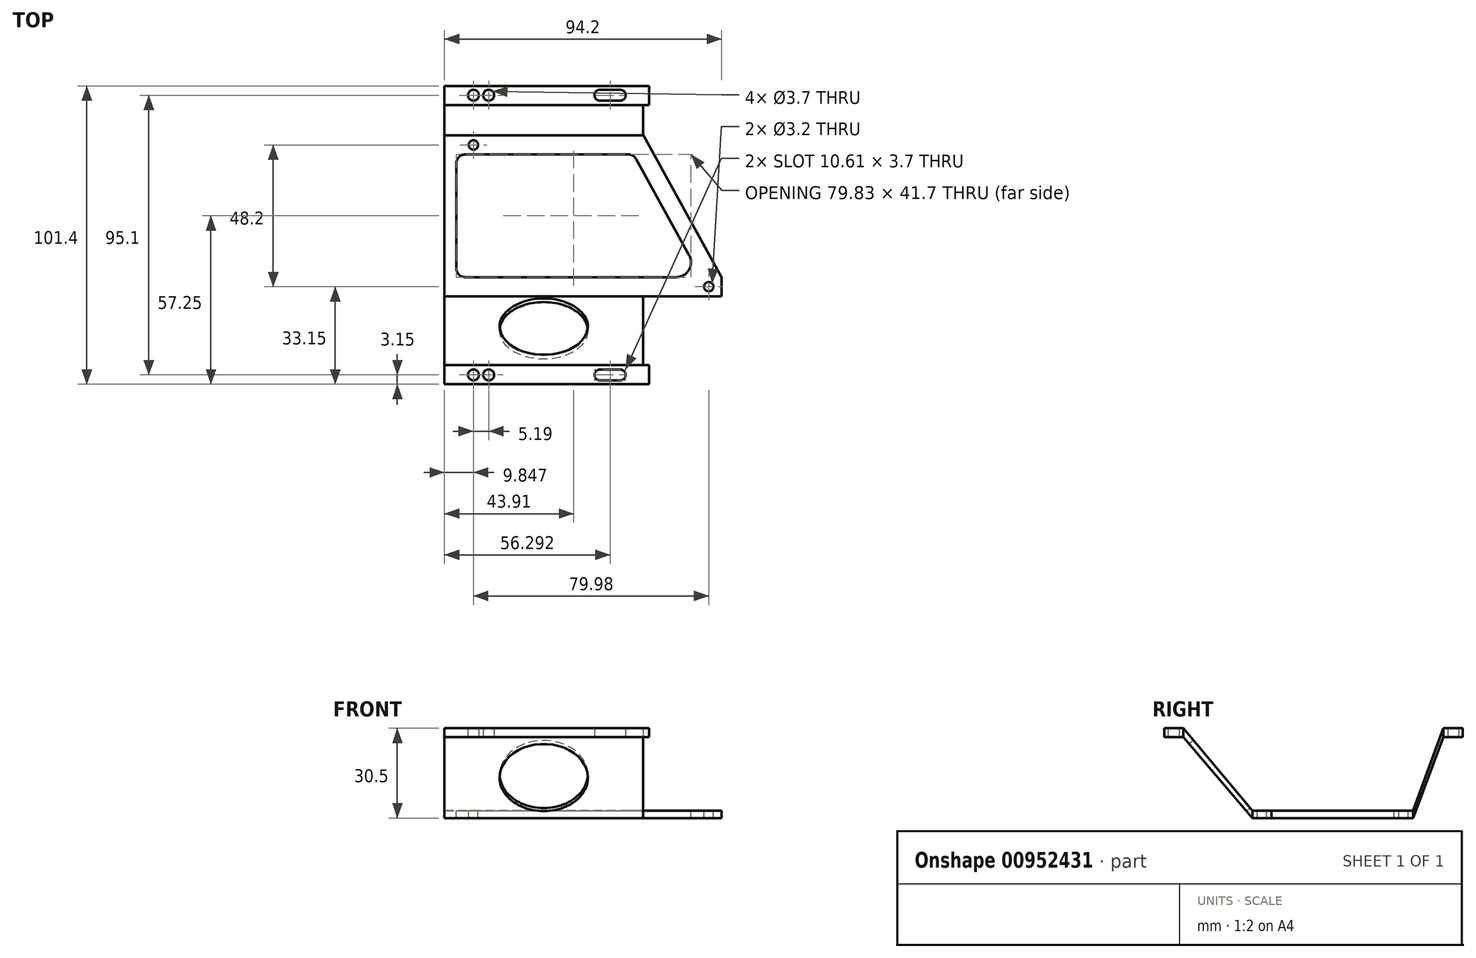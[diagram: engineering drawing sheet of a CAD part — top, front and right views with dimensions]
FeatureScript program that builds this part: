
annotation { "Feature Type Name" : "Feature", "Feature Type Description" : "" }
export const myFeature = defineFeature(function(context is Context, id is Id, definition is map)
    precondition{}
    {
        {
            var Q0;
            Q0=qCreatedBy(makeId("Top.planeOp"),FACE);
            var sketch = newSketch(context, id + "F0", { "sketchPlane" : qUnion([Q0])});
            skLineSegment(sketch, "E0.bottom", {"start": v(-119.45, 40.08) * mm, "end": v(-9.45, 40.08) * mm});
            skLineSegment(sketch, "E0.top", {"start": v(-119.45, -61.32) * mm, "end": v(-9.45, -61.32) * mm});
            skLineSegment(sketch, "E0.left", {"start": v(-119.45, 40.08) * mm, "end": v(-119.45, -61.32) * mm});
            skLineSegment(sketch, "E0.right", {"start": v(-9.45, 40.08) * mm, "end": v(-9.45, -61.32) * mm});
            skLineSegment(sketch, "E1", {"start": v(-119.45, 36.93) * mm, "end": v(-9.45, 36.93) * mm, "construction": true});
            skLineSegment(sketch, "E2", {"start": v(-119.45, -58.17) * mm, "end": v(-9.45, -58.17) * mm, "construction": true});
            skCircle(sketch, "E3", {"center": v(-94.21, 36.93) * mm, "radius": 1.85 * mm});
            skCircle(sketch, "E4", {"center": v(-99.4, 36.93) * mm, "radius": 1.85 * mm});
            skCircle(sketch, "E5", {"center": v(-99.4, -58.17) * mm, "radius": 1.85 * mm});
            skCircle(sketch, "E6", {"center": v(-94.21, -58.17) * mm, "radius": 1.85 * mm});
            skPoint(sketch, "E7", {"position": v(-58.26, 36.93) * mm});
            skPoint(sketch, "E8", {"position": v(-47.65, 36.93) * mm});
            skLineSegment(sketch, "E9", {"start": v(-56.41, 38.78) * mm, "end": v(-49.5, 38.78) * mm});
            skLineSegment(sketch, "E10", {"start": v(-56.41, 35.08) * mm, "end": v(-49.5, 35.08) * mm});
            skLineSegment(sketch, "E11", {"start": v(-56.41, -56.32) * mm, "end": v(-49.5, -56.32) * mm});
            skLineSegment(sketch, "E12", {"start": v(-56.41, -60.02) * mm, "end": v(-49.5, -60.02) * mm});
            skArc(sketch, "E13", {"start": v(-56.41, -56.32) * mm, "mid": v(-58.26, -58.17) * mm, "end": v(-56.41, -60.02) * mm});
            skArc(sketch, "E14", {"start": v(-56.41, -60.02) * mm, "mid": v(-54.56, -58.17) * mm, "end": v(-56.41, -56.32) * mm, "construction": true});
            skArc(sketch, "E15", {"start": v(-49.5, -56.32) * mm, "mid": v(-51.35, -58.17) * mm, "end": v(-49.5, -60.02) * mm, "construction": true});
            skArc(sketch, "E16", {"start": v(-49.5, -60.02) * mm, "mid": v(-47.65, -58.17) * mm, "end": v(-49.5, -56.32) * mm});
            skArc(sketch, "E17", {"start": v(-49.5, 38.78) * mm, "mid": v(-51.35, 36.93) * mm, "end": v(-49.5, 35.08) * mm, "construction": true});
            skArc(sketch, "E18", {"start": v(-49.5, 35.08) * mm, "mid": v(-47.65, 36.93) * mm, "end": v(-49.5, 38.78) * mm});
            skArc(sketch, "E19", {"start": v(-56.41, 35.08) * mm, "mid": v(-54.56, 36.93) * mm, "end": v(-56.41, 38.78) * mm, "construction": true});
            skArc(sketch, "E20", {"start": v(-56.41, 38.78) * mm, "mid": v(-58.26, 36.93) * mm, "end": v(-56.41, 35.08) * mm});
            skPoint(sketch, "E21", {"position": v(-101.25, 36.93) * mm});
            skPoint(sketch, "E22", {"position": v(-97.55, 36.93) * mm});
            skPoint(sketch, "E23", {"position": v(-96.06, 36.93) * mm});
            skPoint(sketch, "E24", {"position": v(-92.36, 36.93) * mm});
            skPoint(sketch, "E25", {"position": v(-99.4, 38.78) * mm});
            skPoint(sketch, "E26", {"position": v(-99.4, -60.02) * mm});
            skSolve(sketch);
        }
        {
            var Q0;
            Q0=qCreatedBy(makeId("Top.planeOp"),FACE);
            cPlane(context, id + "F1", {"entities" : qUnion([Q0]), "cplaneType" : CPlaneType.OFFSET, "offset" : 25 * mm, "width" : 150 * mm, "height" : 150 * mm});
        }
        {
            var Q0;
            Q0=qCreatedBy(id+"F1.planeOp",FACE);
            var sketch = newSketch(context, id + "F2", { "sketchPlane" : qUnion([Q0])});
            skCircle(sketch, "E27.0", {"center": v(-99.4, 36.93) * mm, "radius": 1.85 * mm});
            skCircle(sketch, "E27.1.0", {"center": v(-99.4, 36.93) * mm, "radius": 1.85 * mm});
            skCircle(sketch, "E27.2.0", {"center": v(-94.21, 36.93) * mm, "radius": 1.85 * mm});
            skLineSegment(sketch, "E27.3.0", {"start": v(-119.45, 40.08) * mm, "end": v(-119.45, -61.32) * mm});
            skLineSegment(sketch, "E27.3.1", {"start": v(-119.45, -61.32) * mm, "end": v(-9.45, -61.32) * mm});
            skLineSegment(sketch, "E27.3.2", {"start": v(-9.45, -61.32) * mm, "end": v(-9.45, 40.08) * mm});
            skLineSegment(sketch, "E27.3.3", {"start": v(-9.45, 40.08) * mm, "end": v(-119.45, 40.08) * mm});
            skArc(sketch, "E27.4.0", {"start": v(-56.41, 38.78) * mm, "mid": v(-58.26, 36.93) * mm, "end": v(-56.41, 35.08) * mm});
            skLineSegment(sketch, "E27.4.1", {"start": v(-56.41, 35.08) * mm, "end": v(-49.5, 35.08) * mm});
            skArc(sketch, "E27.4.2", {"start": v(-49.5, 35.08) * mm, "mid": v(-47.65, 36.93) * mm, "end": v(-49.5, 38.78) * mm});
            skLineSegment(sketch, "E27.4.3", {"start": v(-49.5, 38.78) * mm, "end": v(-56.41, 38.78) * mm});
            skCircle(sketch, "E27.5.0", {"center": v(-99.4, -58.17) * mm, "radius": 1.85 * mm});
            skCircle(sketch, "E27.6.0", {"center": v(-94.21, -58.17) * mm, "radius": 1.85 * mm});
            skArc(sketch, "E27.7.0", {"start": v(-56.41, -56.32) * mm, "mid": v(-58.26, -58.17) * mm, "end": v(-56.41, -60.02) * mm});
            skLineSegment(sketch, "E27.7.1", {"start": v(-56.41, -60.02) * mm, "end": v(-49.5, -60.02) * mm});
            skArc(sketch, "E27.7.2", {"start": v(-49.5, -60.02) * mm, "mid": v(-47.65, -58.17) * mm, "end": v(-49.5, -56.32) * mm});
            skLineSegment(sketch, "E27.7.3", {"start": v(-49.5, -56.32) * mm, "end": v(-56.41, -56.32) * mm});
            skLineSegment(sketch, "E28.bottom", {"start": v(-109.25, 40.08) * mm, "end": v(-39.65, 40.08) * mm});
            skLineSegment(sketch, "E28.top", {"start": v(-109.25, 33.58) * mm, "end": v(-39.65, 33.58) * mm});
            skLineSegment(sketch, "E28.left", {"start": v(-109.25, 40.08) * mm, "end": v(-109.25, 33.58) * mm});
            skLineSegment(sketch, "E28.right", {"start": v(-39.65, 40.08) * mm, "end": v(-39.65, 33.58) * mm});
            skPoint(sketch, "E29", {"position": v(-101.25, 36.93) * mm});
            skPoint(sketch, "E30", {"position": v(-47.65, 36.93) * mm});
            skLineSegment(sketch, "E31.bottom", {"start": v(-109.25, -54.82) * mm, "end": v(-39.65, -54.82) * mm});
            skLineSegment(sketch, "E31.top", {"start": v(-109.25, -61.32) * mm, "end": v(-39.65, -61.32) * mm});
            skLineSegment(sketch, "E31.left", {"start": v(-109.25, -54.82) * mm, "end": v(-109.25, -61.32) * mm});
            skLineSegment(sketch, "E31.right", {"start": v(-39.65, -54.82) * mm, "end": v(-39.65, -61.32) * mm});
            skLineSegment(sketch, "E32.bottom", {"start": v(-114.7, 22.63) * mm, "end": v(-13.1, 22.63) * mm, "construction": true});
            skLineSegment(sketch, "E32.top", {"start": v(-114.7, -30.67) * mm, "end": v(-13.1, -30.67) * mm, "construction": true});
            skLineSegment(sketch, "E32.left", {"start": v(-114.7, 22.63) * mm, "end": v(-114.7, -30.67) * mm, "construction": true});
            skLineSegment(sketch, "E32.right", {"start": v(-13.1, 22.63) * mm, "end": v(-13.1, -30.67) * mm, "construction": true});
            skCircle(sketch, "E33", {"center": v(-99.4, 20.03) * mm, "radius": 1.6 * mm});
            skCircle(sketch, "E34", {"center": v(-19.42, -28.17) * mm, "radius": 1.6 * mm});
            skPoint(sketch, "E35", {"position": v(-99.4, 21.63) * mm});
            skPoint(sketch, "E36", {"position": v(-101, 20.03) * mm});
            skPoint(sketch, "E37", {"position": v(-19.42, -29.77) * mm});
            skPoint(sketch, "E38", {"position": v(-17.82, -28.17) * mm});
            skSolve(sketch);
        }
        {
            var Q0;
            Q0=makeQuery(id+"F2.imprint","IMPRINT",FACE,{"disambiguationData":[TD([[makeQuery(id+"F2.imprint","IMPRINT",EDGE,{"derivedFrom":sQuery(id+"F2.wireOp",EDGE,"E27.0")}),-1.0]])]});
            var Q1;
            Q1=makeQuery(id+"F2.imprint","IMPRINT",FACE,{"disambiguationData":[TD([[makeQuery(id+"F2.imprint","IMPRINT",EDGE,{"derivedFrom":sQuery(id+"F2.wireOp",EDGE,"E27.5.0")}),-1.0]])]});
            extrude(context, id + "F3", {"entities" : qUnion([Q0, Q1]), "depth" : 3 * mm, "offsetDistance" : 25 * mm});
        }
        {
            var Q0;
            Q0=qCreatedBy(makeId("Top.planeOp"),FACE);
            var sketch = newSketch(context, id + "F4", { "sketchPlane" : qUnion([Q0])});
            skCircle(sketch, "E39.0", {"center": v(-99.4, 36.93) * mm, "radius": 1.85 * mm});
            skCircle(sketch, "E39.1", {"center": v(-99.4, 36.93) * mm, "radius": 1.85 * mm});
            skCircle(sketch, "E39.2", {"center": v(-94.21, 36.93) * mm, "radius": 1.85 * mm});
            skLineSegment(sketch, "E39.3", {"start": v(-119.45, 40.08) * mm, "end": v(-119.45, -61.32) * mm});
            skLineSegment(sketch, "E39.4", {"start": v(-119.45, -61.32) * mm, "end": v(-9.45, -61.32) * mm});
            skLineSegment(sketch, "E39.5", {"start": v(-9.45, -61.32) * mm, "end": v(-9.45, 40.08) * mm});
            skLineSegment(sketch, "E39.6", {"start": v(-9.45, 40.08) * mm, "end": v(-119.45, 40.08) * mm});
            skArc(sketch, "E39.7", {"start": v(-56.41, 38.78) * mm, "mid": v(-58.26, 36.93) * mm, "end": v(-56.41, 35.08) * mm});
            skLineSegment(sketch, "E39.8", {"start": v(-56.41, 35.08) * mm, "end": v(-49.5, 35.08) * mm});
            skArc(sketch, "E39.9", {"start": v(-49.5, 35.08) * mm, "mid": v(-47.65, 36.93) * mm, "end": v(-49.5, 38.78) * mm});
            skLineSegment(sketch, "E39.10", {"start": v(-49.5, 38.78) * mm, "end": v(-56.41, 38.78) * mm});
            skCircle(sketch, "E39.11", {"center": v(-99.4, -58.17) * mm, "radius": 1.85 * mm});
            skCircle(sketch, "E39.12", {"center": v(-94.21, -58.17) * mm, "radius": 1.85 * mm});
            skArc(sketch, "E39.13", {"start": v(-56.41, -56.32) * mm, "mid": v(-58.26, -58.17) * mm, "end": v(-56.41, -60.02) * mm});
            skLineSegment(sketch, "E39.14", {"start": v(-56.41, -60.02) * mm, "end": v(-49.5, -60.02) * mm});
            skArc(sketch, "E39.15", {"start": v(-49.5, -60.02) * mm, "mid": v(-47.65, -58.17) * mm, "end": v(-49.5, -56.32) * mm});
            skLineSegment(sketch, "E39.16", {"start": v(-49.5, -56.32) * mm, "end": v(-56.41, -56.32) * mm});
            skLineSegment(sketch, "E39.17", {"start": v(-109.25, 40.08) * mm, "end": v(-39.65, 40.08) * mm});
            skLineSegment(sketch, "E39.18", {"start": v(-109.25, 33.58) * mm, "end": v(-39.65, 33.58) * mm});
            skLineSegment(sketch, "E39.19", {"start": v(-109.25, 40.08) * mm, "end": v(-109.25, 33.58) * mm});
            skLineSegment(sketch, "E39.20", {"start": v(-39.65, 40.08) * mm, "end": v(-39.65, 33.58) * mm});
            skPoint(sketch, "E39.21", {"position": v(-101.25, 36.93) * mm});
            skPoint(sketch, "E39.22", {"position": v(-47.65, 36.93) * mm});
            skLineSegment(sketch, "E39.23", {"start": v(-109.25, -54.82) * mm, "end": v(-39.65, -54.82) * mm});
            skLineSegment(sketch, "E39.24", {"start": v(-109.25, -61.32) * mm, "end": v(-39.65, -61.32) * mm});
            skLineSegment(sketch, "E39.25", {"start": v(-109.25, -54.82) * mm, "end": v(-109.25, -61.32) * mm});
            skLineSegment(sketch, "E39.26", {"start": v(-39.65, -54.82) * mm, "end": v(-39.65, -61.32) * mm});
            skLineSegment(sketch, "E39.27", {"start": v(-114.7, 22.63) * mm, "end": v(-13.1, 22.63) * mm, "construction": true});
            skLineSegment(sketch, "E39.28", {"start": v(-114.7, -30.67) * mm, "end": v(-13.1, -30.67) * mm, "construction": true});
            skLineSegment(sketch, "E39.29", {"start": v(-114.7, 22.63) * mm, "end": v(-114.7, -30.67) * mm, "construction": true});
            skLineSegment(sketch, "E39.30", {"start": v(-13.1, 22.63) * mm, "end": v(-13.1, -30.67) * mm, "construction": true});
            skCircle(sketch, "E39.31", {"center": v(-99.4, 20.03) * mm, "radius": 1.6 * mm});
            skCircle(sketch, "E39.32", {"center": v(-19.42, -28.17) * mm, "radius": 1.6 * mm});
            skPoint(sketch, "E39.33", {"position": v(-99.4, 21.63) * mm});
            skPoint(sketch, "E39.34", {"position": v(-101, 20.03) * mm});
            skPoint(sketch, "E39.35", {"position": v(-19.42, -28.17) * mm});
            skPoint(sketch, "E39.36", {"position": v(-19.42, -29.77) * mm});
            skPoint(sketch, "E39.37", {"position": v(-17.82, -28.17) * mm});
            skLineSegment(sketch, "E40.bottom", {"start": v(-109.25, 23.28) * mm, "end": v(-41.64, 23.28) * mm});
            skLineSegment(sketch, "E40.top", {"start": v(-102.25, 16.78) * mm, "end": v(-46.74, 16.78) * mm});
            skLineSegment(sketch, "E40.left", {"start": v(-109.25, 23.28) * mm, "end": v(-109.25, 16.78) * mm});
            skLineSegment(sketch, "E41.bottom", {"start": v(-109.25, -31.42) * mm, "end": v(-15.05, -31.42) * mm});
            skLineSegment(sketch, "E41.top", {"start": v(-102.25, -24.92) * mm, "end": v(-30.43, -24.92) * mm});
            skLineSegment(sketch, "E41.left", {"start": v(-109.25, -31.42) * mm, "end": v(-109.25, -24.92) * mm});
            skLineSegment(sketch, "E41.right", {"start": v(-15.05, -31.42) * mm, "end": v(-15.05, -24.92) * mm});
            skLineSegment(sketch, "E42", {"start": v(-109.25, 16.78) * mm, "end": v(-109.25, -24.92) * mm});
            skLineSegment(sketch, "E43", {"start": v(-105.25, 13.78) * mm, "end": v(-105.25, -21.92) * mm});
            skLineSegment(sketch, "E44", {"start": v(-41.64, 23.28) * mm, "end": v(-15.05, -24.92) * mm});
            skLineSegment(sketch, "E45", {"start": v(-44.1, 15.23) * mm, "end": v(-26.05, -17.5) * mm});
            skPoint(sketch, "E46.visualSharp", {"position": v(-21.96, -24.92) * mm});
            skArc(sketch, "E46.filletArc", {"start": v(-30.43, -24.92) * mm, "mid": v(-26.12, -22.46) * mm, "end": v(-26.05, -17.5) * mm});
            skPoint(sketch, "E47.visualSharp", {"position": v(-44.97, 16.78) * mm});
            skArc(sketch, "E47.filletArc", {"start": v(-44.1, 15.23) * mm, "mid": v(-45.21, 16.36) * mm, "end": v(-46.74, 16.78) * mm});
            skPoint(sketch, "E48.visualSharp", {"position": v(-105.25, 16.78) * mm});
            skArc(sketch, "E48.filletArc", {"start": v(-102.25, 16.78) * mm, "mid": v(-104.37, 15.9) * mm, "end": v(-105.25, 13.78) * mm});
            skPoint(sketch, "E49.visualSharp", {"position": v(-105.25, -24.92) * mm});
            skArc(sketch, "E49.filletArc", {"start": v(-105.25, -21.92) * mm, "mid": v(-104.37, -24.04) * mm, "end": v(-102.25, -24.92) * mm});
            skSolve(sketch);
        }
        {
            var Q0;
            Q0=makeQuery(id+"F3.opExtrude","SWEPT_FACE",FACE,{"disambiguationData":[OSD([sQuery(id+"F2.wireOp",EDGE,"E28.left")])]});
            var sketch = newSketch(context, id + "F5", { "sketchPlane" : qUnion([Q0])});
            skSolve(sketch);
        }
        {
            var Q0;
            Q0=makeQuery(id+"F4.imprint","IMPRINT",FACE,{"disambiguationData":[TD([[makeQuery(id+"F4.imprint","IMPRINT",EDGE,{"derivedFrom":sQuery(id+"F4.wireOp",EDGE,"E39.31")}),-1.0]])]});
            extrude(context, id + "F6", {"entities" : qUnion([Q0]), "oppositeDirection" : true, "depth" : 2.5 * mm, "offsetDistance" : 25 * mm});
        }
        {
            var Q0;
            {var subQ0=sQuery(id+"F2.wireOp",EDGE,"E28.left");Q0=makeQuery(id+"F5.imprint","IMPRINT",FACE,{"disambiguationData":[TD([[makeQuery(id+"F5.imprint","IMPRINT",EDGE,{"derivedFrom":makeQuery(id+"F3.opExtrude","CAP_EDGE",EDGE,{"disambiguationData":[OSD([subQ0])],"isStart":true})}),1.0]])]});}
            var sketch = newSketch(context, id + "F7", { "sketchPlane" : qUnion([Q0])});
            skPoint(sketch, "E50.0", {"position": v(-40.08, 25) * mm});
            skPoint(sketch, "E50.1", {"position": v(-33.58, 25) * mm});
            skPoint(sketch, "E50.2", {"position": v(-33.58, 28) * mm});
            skPoint(sketch, "E50.3", {"position": v(-23.28, 0) * mm});
            skPoint(sketch, "E50.4", {"position": v(-23.28, -2.5) * mm});
            skPoint(sketch, "E50.5", {"position": v(31.42, -2.5) * mm});
            skPoint(sketch, "E50.6", {"position": v(31.42, 0) * mm});
            skPoint(sketch, "E50.7", {"position": v(54.82, 25) * mm});
            skPoint(sketch, "E50.8", {"position": v(54.82, 28) * mm});
            skPoint(sketch, "E50.9", {"position": v(61.32, 25) * mm});
            skLineSegment(sketch, "E51", {"start": v(-33.58, 28) * mm, "end": v(-23.28, 0) * mm});
            skLineSegment(sketch, "E52", {"start": v(-33.58, 25) * mm, "end": v(-23.28, -2.5) * mm});
            skLineSegment(sketch, "E53", {"start": v(31.42, 0) * mm, "end": v(54.82, 28) * mm});
            skLineSegment(sketch, "E54", {"start": v(31.42, -2.5) * mm, "end": v(54.82, 25) * mm});
            skLineSegment(sketch, "E55", {"start": v(-33.58, 28) * mm, "end": v(-33.58, 25) * mm});
            skLineSegment(sketch, "E56", {"start": v(-23.28, 0) * mm, "end": v(-23.28, -2.5) * mm});
            skLineSegment(sketch, "E57", {"start": v(54.82, 28) * mm, "end": v(54.82, 25) * mm});
            skLineSegment(sketch, "E58", {"start": v(31.42, 0) * mm, "end": v(31.42, -2.5) * mm});
            skSolve(sketch);
        }
        {
            var Q0;
            Q0=makeQuery(id+"F7.imprint","IMPRINT",FACE,{"disambiguationData":[TD([[makeQuery(id+"F7.imprint","IMPRINT",EDGE,{"derivedFrom":sQuery(id+"F7.wireOp",EDGE,"E51")}),-1.0]])]});
            var Q1;
            Q1=makeQuery(id+"F7.imprint","IMPRINT",FACE,{"disambiguationData":[TD([[makeQuery(id+"F7.imprint","IMPRINT",EDGE,{"derivedFrom":sQuery(id+"F7.wireOp",EDGE,"E53")}),-1.0]])]});
            extrude(context, id + "F8", {"entities" : qUnion([Q0, Q1]), "oppositeDirection" : true, "depth" : 67.5 * mm, "offsetDistance" : 25 * mm});
        }
        {
            var Q0;
            Q0=makeQuery(id+"F8.opExtrude","SWEPT_FACE",FACE,{"disambiguationData":[OSD([sQuery(id+"F7.wireOp",EDGE,"E54")])]});
            var sketch = newSketch(context, id + "F9", { "sketchPlane" : qUnion([Q0])});
            skLineSegment(sketch, "E59", {"start": v(-75.5, 54.57) * mm, "end": v(-75.5, 18.46) * mm, "construction": true});
            skLineSegment(sketch, "E60", {"start": v(-109.25, 36.51) * mm, "end": v(-41.75, 36.51) * mm, "construction": true});
            skCircle(sketch, "E61", {"center": v(-75.5, 36.51) * mm, "radius": 15 * mm});
            skSolve(sketch);
        }
        {
            var Q0;
            Q0=makeQuery(id+"F9.imprint","IMPRINT",FACE,{"disambiguationData":[TD([[makeQuery(id+"F9.imprint","IMPRINT",EDGE,{"derivedFrom":sQuery(id+"F9.wireOp",EDGE,"E61")}),1.0]])]});
            extrude(context, id + "F10", {"entities" : qUnion([Q0]), "operationType" : NewBodyOperationType.REMOVE, "oppositeDirection" : true, "depth" : 25 * mm, "offsetDistance" : 25 * mm});
        }
    });
